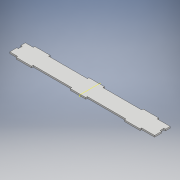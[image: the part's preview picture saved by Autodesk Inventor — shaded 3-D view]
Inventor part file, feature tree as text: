
AUTODESK INVENTOR PART (.ipt)
format: ipt  version: 2018 (Build 220112000, 112)  size: 165,888 bytes
history: native  units: mm
features: extrude x2, sketch x2, plane x1, mirror x1, projected_geometry x1
ambient origin geometry x8: Origin, YZ Plane, XZ Plane, XY Plane, X Axis, Y Axis, Z Axis, Center Point
bodies: Body1 (feature_tree)
feature tree (7):
  extrude  "Extrusion2"  Depth=40.0mm
  extrude  "Extrusion4"  Depth=4.0mm
  plane  "Work Plane1"
  mirror  "Mirror1"
  sketch  "Sketch2"  dims[d2=4.0mm d3=40.0mm]
  sketch  "Sketch4"  dims[d4=4.0mm d5=0.0mm d13=4.0mm d14=10.0mm d15=4.0mm d16=0.0mm]
  projected_geometry  "Projected Loop2"
